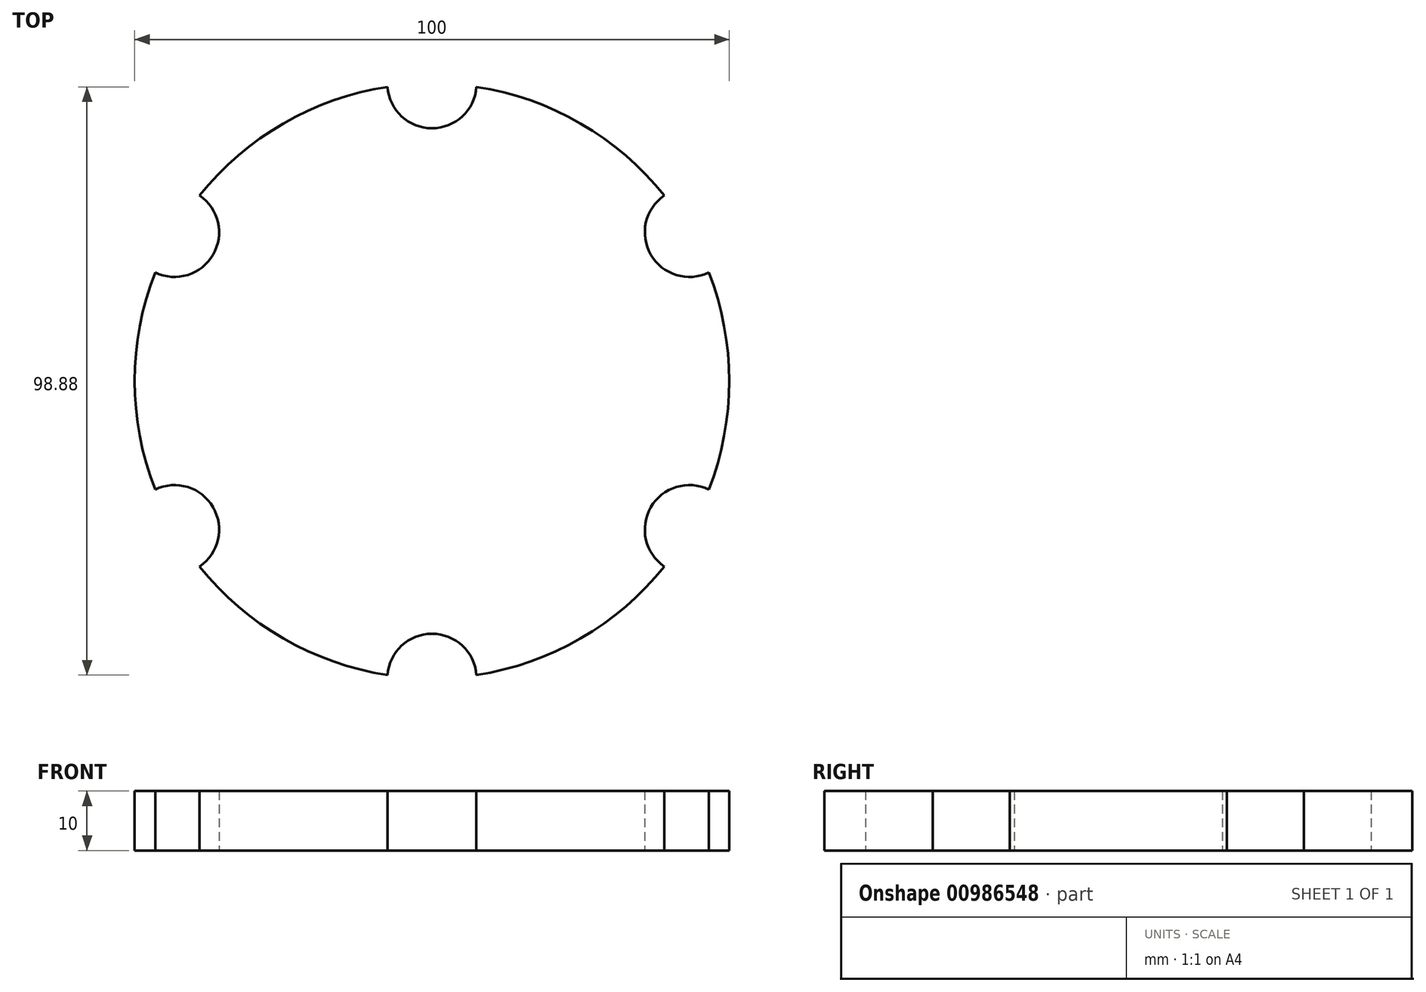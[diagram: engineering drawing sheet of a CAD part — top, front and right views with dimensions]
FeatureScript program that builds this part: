
annotation { "Feature Type Name" : "Feature", "Feature Type Description" : "" }
export const myFeature = defineFeature(function(context is Context, id is Id, definition is map)
    precondition{}
    {
        {
            var Q0;
            Q0=qCreatedBy(makeId("Top.planeOp"),FACE);
            var sketch = newSketch(context, id + "F0", { "sketchPlane" : qUnion([Q0])});
            skCircle(sketch, "E0", {"center": v(0, 0) * mm, "radius": 50 * mm});
            skCircle(sketch, "E1", {"center": v(0, 50) * mm, "radius": 7.5 * mm});
            skCircle(sketch, "E2", {"center": v(43.3, 25) * mm, "radius": 7.5 * mm});
            skCircle(sketch, "E3", {"center": v(43.3, -25) * mm, "radius": 7.5 * mm});
            skCircle(sketch, "E4", {"center": v(0, -50) * mm, "radius": 7.5 * mm});
            skCircle(sketch, "E5", {"center": v(-43.3, -25) * mm, "radius": 7.5 * mm});
            skCircle(sketch, "E6", {"center": v(-43.3, 25) * mm, "radius": 7.5 * mm});
            skSolve(sketch);
        }
        {
            var Q0;
            {var subQ1=sQuery(id+"F0.wireOp",EDGE,"E0");var subQ12=sQuery(id+"F0.wireOp",EDGE,"E6");var subQ13=makeQuery(id+"F0.imprint","INTERSECT",VERTEX,{"disambiguationData":[OD(0.0)],"derivedFrom":[subQ1,subQ12]});var subQ19=makeQuery(id+"F0.imprint","IMPRINT",FACE,{"disambiguationData":[TD([[makeQuery(id+"F0.imprint","IMPRINT",EDGE,{"disambiguationData":[TD([[subQ13,1.0]])],"derivedFrom":subQ1}),1.0]])]});Q0=qUnion([subQ19,subQ19,subQ19,subQ19,subQ19,subQ19]);}
            extrude(context, id + "F1", {"entities" : qUnion([Q0]), "depth" : 10 * mm, "offsetDistance" : 25.4 * mm});
        }
    });
